# Revit family: L-75-M
name_source: partatom
category: Plumbing Fixtures
revit_build: Autodesk Revit MEP 2016 (Build: 20150220_1215(x64)
units: mm (PartAtom-declared; Revit-internal decimal feet)

## family parameters
Cut with Voids When Loaded = No
Host = Face
OmniClass Number = 23.45.05.17.17
OmniClass Title = Leisure Whirlpools
Part Type = Normal
Room Calculation Point = No
Round Connector Dimension = Use Diameter
Shared = Yes

## types (1)
- L-75-M
    115 VAC / 50Hz    Country of Use = No
    115 VAC / 60Hz    Country of Use = No
    230 VAC / 50Hz     Country of Use = No
    230 VAC / 60Hz     Country of Use = No
    ADH- Auxillary Drain Hose Assembly = No
    ALC- Adjustable Low Chair = No
    ALS - ALC- Adjustable Low Stool = No
    ARS- Arm Rest Support = No
    AS3- Adjustable Suspension Seat = No
    Amperage = 0
    CTS3- Combination Table with Side Seats = No
    CW Connection = No
    Default Elevation = 0"
    Description = 75 Gallon L Series Mobil Whirlpool
    EG- Enviro Glaze Color Powder Coating- Specify Color (Special Finishes Consult Facrtory) = No
    GFI- Ground Fault Interrupter = No
    HR - Head Rest, Adjustable = No
    HW Connection = No
    Hertz = 50
    L-75-M 75 Gallon Mobil Whirlpool = Yes
    Manufacturer = Whitehall
    Material = Type 304 Stainless Steel
    Model = L-75-M
    PCS- Pump Strainer Cover = No
    PHS2- Patient Handling System (Chair Type) = No
    RHG- Rubber Hand Grips = No
    Revised Date = 05/23/19
    SDO- Separate Drain and Overflow Assembly = No
    SDP - Separate Drain Pump = No
    TTS2- Tank Top Seat = No
    Tempered Water Connection = No
    URL = http://www.whitehallmfg.com
    Vent Connection = No
    Voltage = 115
    Waste Connection = Yes

## geometry (parser evidence)
native form markers: Sweep x32
no freeform markers — native parametric forms only
